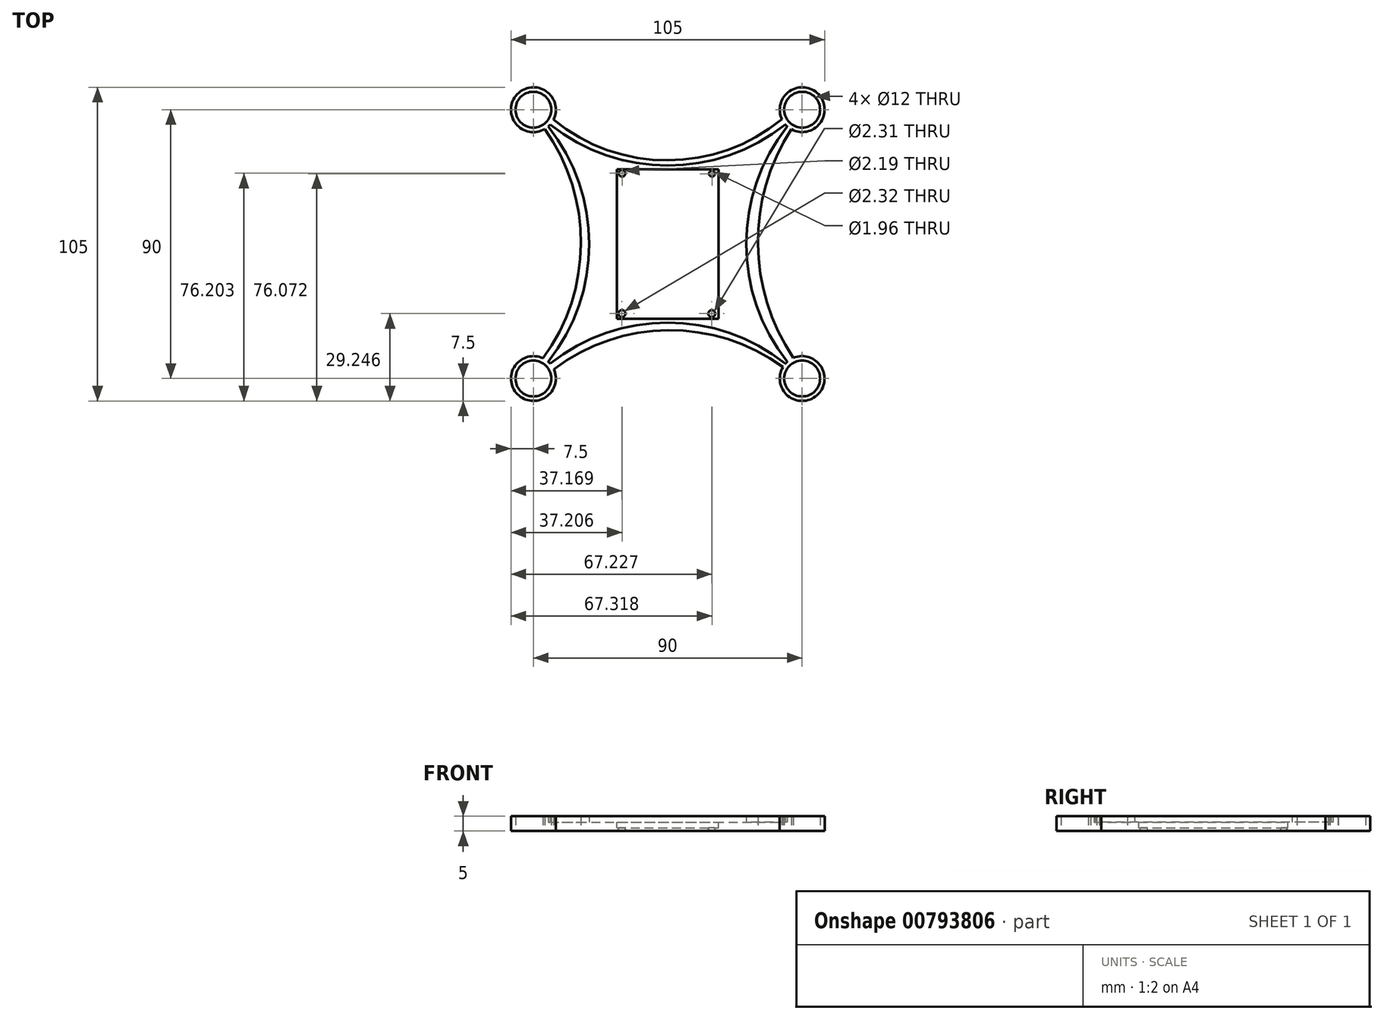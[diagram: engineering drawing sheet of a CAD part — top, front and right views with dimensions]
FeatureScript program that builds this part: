
annotation { "Feature Type Name" : "Feature", "Feature Type Description" : "" }
export const myFeature = defineFeature(function(context is Context, id is Id, definition is map)
    precondition{}
    {
        {
            var Q0;
            Q0=qCreatedBy(makeId("Top.planeOp"),FACE);
            var sketch = newSketch(context, id + "F0", { "sketchPlane" : qUnion([Q0])});
            skLineSegment(sketch, "E0.bottom", {"start": v(0, 0) * mm, "end": v(90, 0) * mm, "construction": true});
            skLineSegment(sketch, "E0.top", {"start": v(0, 90) * mm, "end": v(90, 90) * mm, "construction": true});
            skLineSegment(sketch, "E0.left", {"start": v(0, 0) * mm, "end": v(0, 90) * mm, "construction": true});
            skLineSegment(sketch, "E0.right", {"start": v(90, 0) * mm, "end": v(90, 90) * mm, "construction": true});
            skCircle(sketch, "E1", {"center": v(0, 90) * mm, "radius": 6 * mm});
            skCircle(sketch, "E2", {"center": v(90, 90) * mm, "radius": 6 * mm});
            skCircle(sketch, "E3", {"center": v(90, 0) * mm, "radius": 6 * mm});
            skCircle(sketch, "E4", {"center": v(0, 0) * mm, "radius": 6 * mm});
            skArc(sketch, "E5", {"start": v(6.71, 86.65) * mm, "mid": v(-5.48, 95.12) * mm, "end": v(3.8, 83.53) * mm});
            skArc(sketch, "E6", {"start": v(86.36, 83.44) * mm, "mid": v(95.48, 95.12) * mm, "end": v(83.21, 86.8) * mm});
            skArc(sketch, "E7", {"start": v(85, 5.6) * mm, "mid": v(84.7, 5.3) * mm, "end": v(84.4, 5) * mm});
            skArc(sketch, "E8", {"start": v(5.6, 5) * mm, "mid": v(5.3, 5.3) * mm, "end": v(5, 5.6) * mm});
            skArc(sketch, "E9", {"start": v(90, 90) * mm, "mid": v(89.9, 89.9) * mm, "end": v(89.8, 89.8) * mm});
            skArc(sketch, "E10", {"start": v(90, 0) * mm, "mid": v(89.9, 0.1) * mm, "end": v(89.8, 0.2) * mm});
            skArc(sketch, "E11", {"start": v(0, 0) * mm, "mid": v(0.1, 0.1) * mm, "end": v(0.2, 0.2) * mm});
            skArc(sketch, "E12.trimOffspring", {"start": v(5.6, 85) * mm, "mid": v(45, 71.3) * mm, "end": v(84.4, 85) * mm});
            skArc(sketch, "E13", {"start": v(6.71, 86.65) * mm, "mid": v(44.99, 73.05) * mm, "end": v(83.21, 86.8) * mm});
            skArc(sketch, "E14", {"start": v(86.36, 83.44) * mm, "mid": v(75.18, 45.07) * mm, "end": v(87.07, 6.9) * mm});
            skArc(sketch, "E15", {"start": v(3.24, 6.76) * mm, "mid": v(15.91, 45.06) * mm, "end": v(3.8, 83.53) * mm});
            skArc(sketch, "E16", {"start": v(83.59, 3.89) * mm, "mid": v(45.08, 16.17) * mm, "end": v(6.83, 3.1) * mm});
            skArc(sketch, "E17.trimOffspring", {"start": v(85, 84.4) * mm, "mid": v(71.3, 45) * mm, "end": v(85, 5.6) * mm});
            skArc(sketch, "E18.trimOffspring", {"start": v(89.8, 89.8) * mm, "mid": v(89.9, 89.9) * mm, "end": v(90, 90) * mm});
            skArc(sketch, "E19.trimOffspring", {"start": v(0.2, 0.2) * mm, "mid": v(0.1, 0.1) * mm, "end": v(0, 0) * mm});
            skArc(sketch, "E20.trimOffspring", {"start": v(5, 5.6) * mm, "mid": v(18.7, 45) * mm, "end": v(5, 84.4) * mm});
            skArc(sketch, "E21.trimOffspring", {"start": v(84.4, 5) * mm, "mid": v(45, 18.7) * mm, "end": v(5.6, 5) * mm});
            skArc(sketch, "E22.trimOffspring", {"start": v(89.8, 0.2) * mm, "mid": v(89.9, 0.1) * mm, "end": v(90, 0) * mm});
            skArc(sketch, "E23.trimOffspring", {"start": v(84.4, 85) * mm, "mid": v(84.7, 84.7) * mm, "end": v(85, 84.4) * mm});
            skArc(sketch, "E24.trimOffspring", {"start": v(83.59, 3.89) * mm, "mid": v(94.91, -5.67) * mm, "end": v(87.07, 6.9) * mm});
            skArc(sketch, "E25.trimOffspring", {"start": v(5, 84.4) * mm, "mid": v(5.3, 84.7) * mm, "end": v(5.6, 85) * mm});
            skArc(sketch, "E26.trimOffspring", {"start": v(3.24, 6.76) * mm, "mid": v(-5.36, -5.25) * mm, "end": v(6.83, 3.1) * mm});
            skSolve(sketch);
        }
        {
            var Q0;
            Q0=makeQuery(id+"F0.imprint","IMPRINT",FACE,{"disambiguationData":[TD([[makeQuery(id+"F0.imprint","IMPRINT",EDGE,{"derivedFrom":sQuery(id+"F0.wireOp",EDGE,"E1")}),-1.0]])]});
            extrude(context, id + "F1", {"entities" : qUnion([Q0]), "depth" : 5 * mm, "offsetDistance" : 25.4 * mm});
        }
        {
            var Q0;
            Q0=makeQuery(id+"F0.imprint","IMPRINT",FACE,{"disambiguationData":[TD([[makeQuery(id+"F0.imprint","IMPRINT",EDGE,{"derivedFrom":sQuery(id+"F0.wireOp",EDGE,"E7")}),-1.0]])]});
            extrude(context, id + "F2", {"entities" : qUnion([Q0]), "operationType" : NewBodyOperationType.ADD, "depth" : 3 * mm, "offsetDistance" : 25.4 * mm});
        }
        {
            var Q0;
            Q0=makeQuery(id+"F2.opExtrude","CAP_FACE",FACE,{"disambiguationData":[OSD([sQuery(id+"F0.wireOp",EDGE,"E7"),sQuery(id+"F0.wireOp",EDGE,"E8"),sQuery(id+"F0.wireOp",EDGE,"E12.trimOffspring"),sQuery(id+"F0.wireOp",EDGE,"E17.trimOffspring"),sQuery(id+"F0.wireOp",EDGE,"E20.trimOffspring"),sQuery(id+"F0.wireOp",EDGE,"E21.trimOffspring"),sQuery(id+"F0.wireOp",EDGE,"E23.trimOffspring"),sQuery(id+"F0.wireOp",EDGE,"E25.trimOffspring")])],"isStart":false});
            var sketch = newSketch(context, id + "F3", { "sketchPlane" : qUnion([Q0])});
            skLineSegment(sketch, "E27", {"start": v(62, 20) * mm, "end": v(62, 70) * mm});
            skLineSegment(sketch, "E28", {"start": v(28, 20) * mm, "end": v(28, 70) * mm});
            skLineSegment(sketch, "E29", {"start": v(28, 70) * mm, "end": v(62, 70) * mm});
            skLineSegment(sketch, "E30", {"start": v(28, 20) * mm, "end": v(62, 20) * mm});
            skSolve(sketch);
        }
        {
            var Q0;
            Q0 = qSketchRegion(id + "F3", true);
            extrude(context, id + "F4", {"entities" : qUnion([Q0]), "operationType" : NewBodyOperationType.REMOVE, "oppositeDirection" : true, "depth" : 2 * mm, "offsetDistance" : 25.4 * mm});
        }
        {
            var Q0;
            Q0=makeQuery(id+"F3.imprint","IMPRINT",FACE,{"disambiguationData":[TD([[makeQuery(id+"F3.imprint","IMPRINT",EDGE,{"derivedFrom":sQuery(id+"F3.wireOp",EDGE,"E27")}),1.0]])]});
            var sketch = newSketch(context, id + "F5", { "sketchPlane" : qUnion([Q0])});
            skLineSegment(sketch, "E31", {"start": v(27.96, 26.85) * mm, "end": v(32.95, 20.08) * mm});
            skLineSegment(sketch, "E32", {"start": v(28.02, 64.2) * mm, "end": v(33.44, 70.2) * mm});
            skLineSegment(sketch, "E33", {"start": v(56.12, 70.06) * mm, "end": v(61.83, 63.12) * mm});
            skLineSegment(sketch, "E34", {"start": v(54.5, 20.2) * mm, "end": v(61.83, 25.92) * mm});
            skLineSegment(sketch, "E35", {"start": v(32.95, 20.08) * mm, "end": v(27.9, 20.08) * mm});
            skLineSegment(sketch, "E36", {"start": v(27.96, 26.85) * mm, "end": v(27.9, 20.08) * mm});
            skLineSegment(sketch, "E37", {"start": v(54.5, 20.2) * mm, "end": v(61.83, 20.08) * mm});
            skLineSegment(sketch, "E38", {"start": v(61.83, 25.92) * mm, "end": v(61.83, 20.08) * mm});
            skLineSegment(sketch, "E39", {"start": v(61.83, 63.12) * mm, "end": v(61.83, 70.06) * mm});
            skLineSegment(sketch, "E40", {"start": v(56.12, 70.06) * mm, "end": v(61.83, 70.06) * mm});
            skLineSegment(sketch, "E41", {"start": v(28.02, 64.2) * mm, "end": v(28.02, 70.06) * mm});
            skLineSegment(sketch, "E42", {"start": v(33.44, 70.2) * mm, "end": v(28.02, 70.06) * mm});
            skCircle(sketch, "E43", {"center": v(29.7, 68.7) * mm, "radius": 1.1 * mm});
            skCircle(sketch, "E44", {"center": v(29.67, 21.75) * mm, "radius": 1.16 * mm});
            skCircle(sketch, "E45", {"center": v(59.73, 21.75) * mm, "radius": 1.16 * mm});
            skCircle(sketch, "E46", {"center": v(59.82, 68.57) * mm, "radius": 0.98 * mm});
            skSolve(sketch);
        }
        {
            var Q0;
            Q0=makeQuery(id+"F5.imprint","IMPRINT",FACE,{"disambiguationData":[TD([[makeQuery(id+"F5.imprint","IMPRINT",EDGE,{"derivedFrom":sQuery(id+"F5.wireOp",EDGE,"E45")}),1.0]])]});
            var Q1;
            Q1=makeQuery(id+"F5.imprint","IMPRINT",FACE,{"disambiguationData":[TD([[makeQuery(id+"F5.imprint","IMPRINT",EDGE,{"derivedFrom":sQuery(id+"F5.wireOp",EDGE,"E43")}),1.0]])]});
            var Q2;
            Q2=makeQuery(id+"F5.imprint","IMPRINT",FACE,{"disambiguationData":[TD([[makeQuery(id+"F5.imprint","IMPRINT",EDGE,{"derivedFrom":sQuery(id+"F5.wireOp",EDGE,"E44")}),1.0]])]});
            var Q3;
            Q3=makeQuery(id+"F5.imprint","IMPRINT",FACE,{"disambiguationData":[TD([[makeQuery(id+"F5.imprint","IMPRINT",EDGE,{"derivedFrom":sQuery(id+"F5.wireOp",EDGE,"E46")}),1.0]])]});
            extrude(context, id + "F6", {"entities" : qUnion([Q0, Q1, Q2, Q3]), "operationType" : NewBodyOperationType.REMOVE, "endBound" : BoundingType.THROUGH_ALL, "oppositeDirection" : true, "depth" : 3 * mm, "offsetDistance" : 25.4 * mm});
        }
    });
